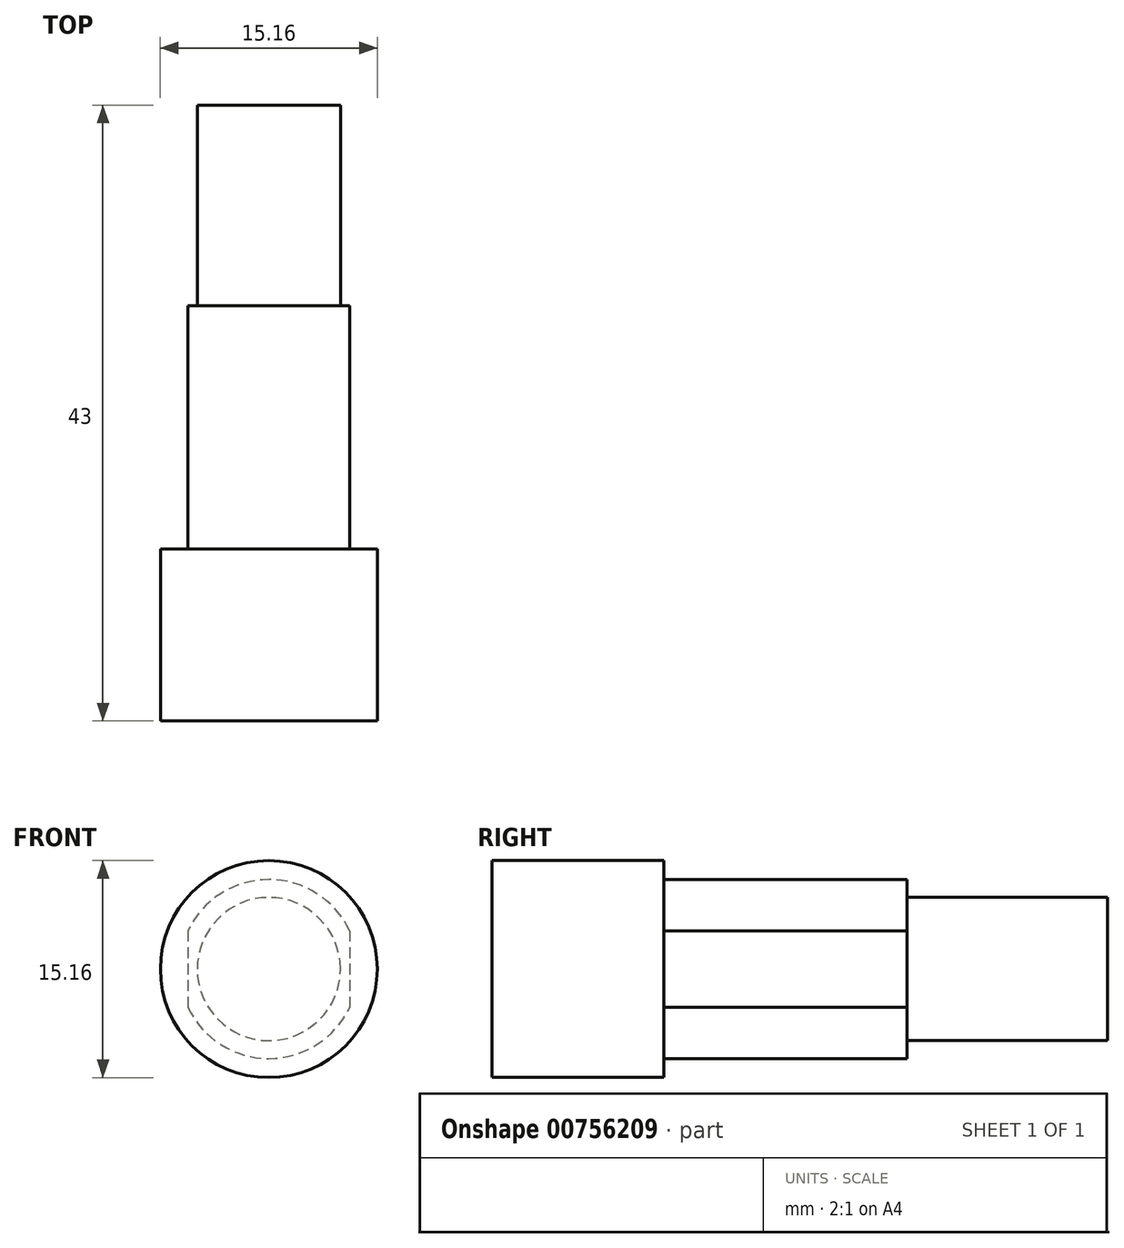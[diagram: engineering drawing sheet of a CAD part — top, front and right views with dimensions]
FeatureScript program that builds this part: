
annotation { "Feature Type Name" : "Feature", "Feature Type Description" : "" }
export const myFeature = defineFeature(function(context is Context, id is Id, definition is map)
    precondition{}
    {
        {
            var Q0;
            Q0=qCreatedBy(makeId("Front.planeOp"),FACE);
            var sketch = newSketch(context, id + "F0", { "sketchPlane" : qUnion([Q0])});
            skCircle(sketch, "E0", {"center": v(0, 0) * mm, "radius": 6.25 * mm});
            skSolve(sketch);
        }
        {
            var Q0;
            Q0=qSketchRegion(id+"F0",true);
            extrude(context, id + "F1", {"entities" : qUnion([Q0]), "depth" : 17 * mm, "offsetDistance" : 25 * mm});
        }
        {
            var Q0;
            Q0=makeQuery(id+"F1.opExtrude","CAP_FACE",FACE,{"disambiguationData":[OSD([sQuery(id+"F0.wireOp",EDGE,"E0")])],"isStart":false});
            var sketch = newSketch(context, id + "F2", { "sketchPlane" : qUnion([Q0])});
            skCircle(sketch, "E1", {"center": v(0, 0) * mm, "radius": 7.58 * mm});
            skSolve(sketch);
        }
        {
            var Q0;
            Q0=qSketchRegion(id+"F2",true);
            extrude(context, id + "F3", {"entities" : qUnion([Q0]), "operationType" : NewBodyOperationType.ADD, "depth" : 12 * mm, "offsetDistance" : 25 * mm});
        }
        {
            var Q0;
            Q0=makeQuery(id+"F1.opExtrude","CAP_FACE",FACE,{"disambiguationData":[OSD([sQuery(id+"F0.wireOp",EDGE,"E0")])],"isStart":true});
            var sketch = newSketch(context, id + "F4", { "sketchPlane" : qUnion([Q0])});
            skLineSegment(sketch, "E2.bottom", {"start": v(-5.65, 7.5) * mm, "end": v(5.65, 7.5) * mm});
            skLineSegment(sketch, "E2.top", {"start": v(-5.65, -7.5) * mm, "end": v(5.65, -7.5) * mm});
            skLineSegment(sketch, "E2.left", {"start": v(-5.65, 7.5) * mm, "end": v(-5.65, -7.5) * mm});
            skLineSegment(sketch, "E2.right", {"start": v(5.65, 7.5) * mm, "end": v(5.65, -7.5) * mm});
            skPoint(sketch, "E2.middle", {"position": v(0, 0) * mm});
            skLineSegment(sketch, "E3.bottom", {"start": v(-5.65, 7.5) * mm, "end": v(-10.65, 7.5) * mm});
            skLineSegment(sketch, "E3.top", {"start": v(-5.65, -7.5) * mm, "end": v(-10.65, -7.5) * mm});
            skLineSegment(sketch, "E3.right", {"start": v(-10.65, 7.5) * mm, "end": v(-10.65, -7.5) * mm});
            skLineSegment(sketch, "E4.bottom", {"start": v(5.65, 7.5) * mm, "end": v(10.65, 7.5) * mm});
            skLineSegment(sketch, "E4.top", {"start": v(5.65, -7.5) * mm, "end": v(10.65, -7.5) * mm});
            skLineSegment(sketch, "E4.right", {"start": v(10.65, 7.5) * mm, "end": v(10.65, -7.5) * mm});
            skSolve(sketch);
        }
        {
            var Q0;
            {var subQ0=sQuery(id+"F4.wireOp",EDGE,"E2.left");var subQ1=makeQuery(id+"F1.opExtrude","CAP_EDGE",EDGE,{"disambiguationData":[OSD([sQuery(id+"F0.wireOp",EDGE,"E0")])],"isStart":true});var subQ2=makeQuery(id+"F4.imprint","INTERSECT",VERTEX,{"disambiguationData":[OD(0.0)],"derivedFrom":[subQ1,subQ0]});Q0=makeQuery(id+"F4.imprint","IMPRINT",FACE,{"disambiguationData":[TD([[makeQuery(id+"F4.imprint","IMPRINT",EDGE,{"disambiguationData":[TD([[subQ2,-1.0]])],"derivedFrom":subQ0}),-1.0]])]});}
            var Q1;
            {var subQ0=sQuery(id+"F4.wireOp",EDGE,"E2.right");var subQ1=makeQuery(id+"F1.opExtrude","CAP_EDGE",EDGE,{"disambiguationData":[OSD([sQuery(id+"F0.wireOp",EDGE,"E0")])],"isStart":true});var subQ2=makeQuery(id+"F4.imprint","INTERSECT",VERTEX,{"disambiguationData":[OD(0.0)],"derivedFrom":[subQ1,subQ0]});Q1=makeQuery(id+"F4.imprint","IMPRINT",FACE,{"disambiguationData":[TD([[makeQuery(id+"F4.imprint","IMPRINT",EDGE,{"disambiguationData":[TD([[subQ2,-1.0]])],"derivedFrom":subQ0}),1.0]])]});}
            var Q2;
            Q2=makeQuery(id+"F3.opExtrude","CAP_FACE",FACE,{"disambiguationData":[OSD([sQuery(id+"F2.wireOp",EDGE,"E1")])],"isStart":true});
            extrude(context, id + "F5", {"entities" : qUnion([Q0, Q1]), "operationType" : NewBodyOperationType.REMOVE, "endBound" : BoundingType.UP_TO_SURFACE, "oppositeDirection" : true, "depth" : 25 * mm, "endBoundEntityFace" : qUnion([Q2]), "offsetDistance" : 25 * mm});
        }
        {
            var Q0;
            Q0=makeQuery(id+"F1.opExtrude","CAP_FACE",FACE,{"disambiguationData":[OSD([sQuery(id+"F0.wireOp",EDGE,"E0")])],"isStart":true});
            var sketch = newSketch(context, id + "F6", { "sketchPlane" : qUnion([Q0])});
            skCircle(sketch, "E5", {"center": v(0, 0) * mm, "radius": 5 * mm});
            skSolve(sketch);
        }
        {
            var Q0;
            Q0=qSketchRegion(id+"F6",true);
            extrude(context, id + "F7", {"entities" : qUnion([Q0]), "operationType" : NewBodyOperationType.ADD, "depth" : 14 * mm, "offsetDistance" : 25 * mm});
        }
    });
